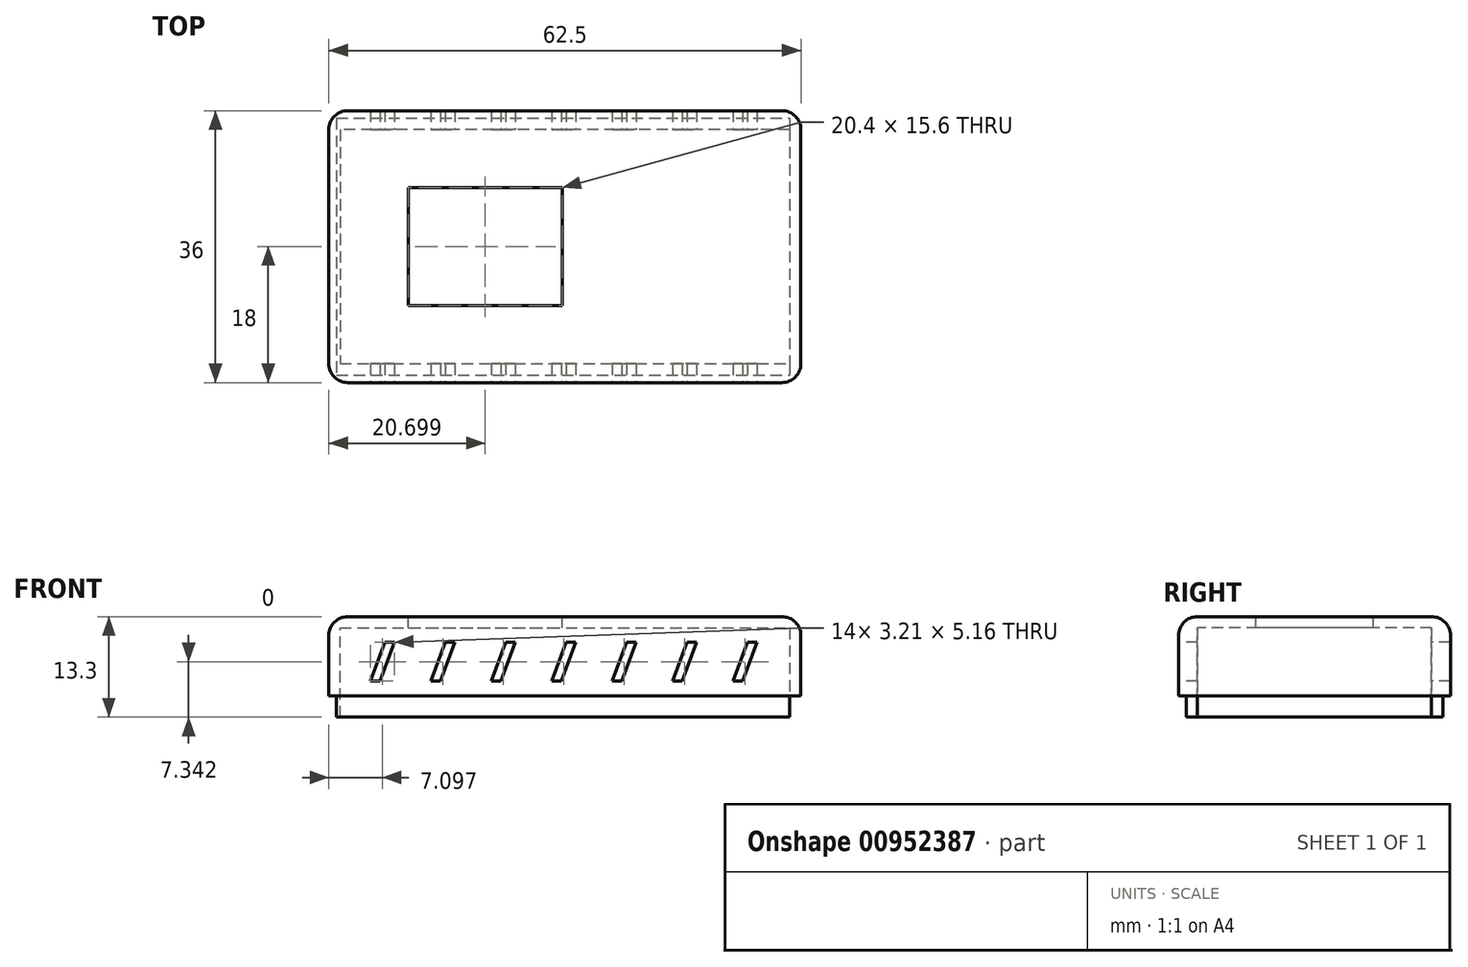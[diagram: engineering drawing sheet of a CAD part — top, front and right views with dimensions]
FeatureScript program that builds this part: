
annotation { "Feature Type Name" : "Feature", "Feature Type Description" : "" }
export const myFeature = defineFeature(function(context is Context, id is Id, definition is map)
    precondition{}
    {
        {
            var Q0;
            Q0=qCreatedBy(makeId("Top.planeOp"),FACE);
            var sketch = newSketch(context, id + "F0", { "sketchPlane" : qUnion([Q0])});
            skLineSegment(sketch, "E0.bottom", {"start": v(-31.16, 18) * mm, "end": v(31.34, 18) * mm});
            skLineSegment(sketch, "E0.top", {"start": v(-31.16, -18) * mm, "end": v(31.34, -18) * mm});
            skLineSegment(sketch, "E0.left", {"start": v(-31.16, 18) * mm, "end": v(-31.16, -18) * mm});
            skLineSegment(sketch, "E0.right", {"start": v(31.34, 18) * mm, "end": v(31.34, -18) * mm});
            skLineSegment(sketch, "E1.bottom", {"start": v(-30.16, 17) * mm, "end": v(29.84, 17) * mm});
            skLineSegment(sketch, "E1.top", {"start": v(-30.16, -17) * mm, "end": v(29.84, -17) * mm});
            skLineSegment(sketch, "E1.left", {"start": v(-30.16, 17) * mm, "end": v(-30.16, -17) * mm});
            skLineSegment(sketch, "E1.right", {"start": v(29.84, 17) * mm, "end": v(29.84, -17) * mm});
            skLineSegment(sketch, "E2", {"start": v(29.84, 15.5) * mm, "end": v(-28.66, 15.5) * mm});
            skLineSegment(sketch, "E3", {"start": v(-28.66, 15.5) * mm, "end": v(-28.66, -15.5) * mm});
            skLineSegment(sketch, "E4", {"start": v(-28.66, -15.5) * mm, "end": v(29.84, -15.5) * mm});
            skSolve(sketch);
        }
        {
            var Q0;
            {var subQ1=sQuery(id+"F0.wireOp",EDGE,"E1.bottom");Q0=makeQuery(id+"F0.imprint","IMPRINT",FACE,{"disambiguationData":[TD([[makeQuery(id+"F0.imprint","IMPRINT",EDGE,{"derivedFrom":subQ1}),-1.0]])]});}
            extrude(context, id + "F1", {"entities" : qUnion([Q0]), "oppositeDirection" : true, "offsetDistance" : 25 * mm, "depth" : 2.8 * mm});
        }
        {
            var Q0;
            Q0=makeQuery(id+"F0.imprint","IMPRINT",FACE,{"disambiguationData":[TD([[makeQuery(id+"F0.imprint","IMPRINT",EDGE,{"derivedFrom":sQuery(id+"F0.wireOp",EDGE,"E0.bottom")}),-1.0]])]});
            var Q1;
            {var subQ1=sQuery(id+"F0.wireOp",EDGE,"E1.bottom");Q1=makeQuery(id+"F0.imprint","IMPRINT",FACE,{"disambiguationData":[TD([[makeQuery(id+"F0.imprint","IMPRINT",EDGE,{"derivedFrom":subQ1}),-1.0]])]});}
            extrude(context, id + "F2", {"entities" : qUnion([Q0, Q1]), "operationType" : NewBodyOperationType.ADD, "offsetDistance" : 25 * mm, "depth" : 9 * mm});
        }
        {
            var Q0;
            Q0=makeQuery(id+"F2.opExtrude","SWEPT_FACE",FACE,{"disambiguationData":[OSD([sQuery(id+"F0.wireOp",EDGE,"E0.right")])]});
            var sketch = newSketch(context, id + "F3", { "sketchPlane" : qUnion([Q0])});
            skLineSegment(sketch, "E5.bottom", {"start": v(-18, 9) * mm, "end": v(18, 9) * mm});
            skLineSegment(sketch, "E5.top", {"start": v(-18, 10.5) * mm, "end": v(18, 10.5) * mm});
            skLineSegment(sketch, "E5.left", {"start": v(-18, 9) * mm, "end": v(-18, 10.5) * mm});
            skLineSegment(sketch, "E5.right", {"start": v(18, 9) * mm, "end": v(18, 10.5) * mm});
            skSolve(sketch);
        }
        {
            var Q0;
            Q0=makeQuery(id+"F3.imprint","IMPRINT",FACE,{"disambiguationData":[TD([[makeQuery(id+"F3.imprint","IMPRINT",EDGE,{"derivedFrom":sQuery(id+"F3.wireOp",EDGE,"E5.bottom")}),-1.0]])]});
            var Q1;
            Q1=qSketchRegion(id+"FGHyg4ucGbV6FiT_1",true);
            var Q2;
            Q2=makeQuery(id+"F2.opExtrude","SWEPT_FACE",FACE,{"disambiguationData":[OSD([sQuery(id+"F0.wireOp",EDGE,"E0.left")])]});
            extrude(context, id + "F4", {"entities" : qUnion([Q0, Q1]), "operationType" : NewBodyOperationType.ADD, "endBound" : BoundingType.UP_TO_SURFACE, "oppositeDirection" : true, "endBoundEntityFace" : qUnion([Q2]), "depth" : 62.3 * mm});
        }
        {
            var Q0;
            Q0=makeQuery(id+"F4.opExtrude","CAP_EDGE",EDGE,{"disambiguationData":[OSD([sQuery(id+"F3.wireOp",EDGE,"E5.top")])],"isStart":true});
            var Q1;
            Q1=makeQuery(id+"F4.opExtrude","SWEPT_EDGE",EDGE,{"disambiguationData":[OSD([sQuery(id+"F3.wireOp",EDGE,"E5.top"),sQuery(id+"F3.wireOp",EDGE,"E5.left")])]});
            var Q2;
            Q2=makeQuery(id+"F4.boolean.opBoolean","MERGE",EDGE,{"derivedFrom":[makeQuery(id+"F2.opExtrude","SWEPT_EDGE",EDGE,{"disambiguationData":[OSD([sQuery(id+"F0.wireOp",EDGE,"E0.top"),sQuery(id+"F0.wireOp",EDGE,"E0.right")])]}),makeQuery(id+"F4.opExtrude","CAP_EDGE",EDGE,{"disambiguationData":[OSD([sQuery(id+"F3.wireOp",EDGE,"E5.left")])],"isStart":true})]});
            var Q3;
            Q3=makeQuery(id+"F4.boolean.opBoolean","MERGE",EDGE,{"derivedFrom":[makeQuery(id+"F2.opExtrude","SWEPT_EDGE",EDGE,{"disambiguationData":[OSD([sQuery(id+"F0.wireOp",EDGE,"E0.bottom"),sQuery(id+"F0.wireOp",EDGE,"E0.right")])]}),makeQuery(id+"F4.opExtrude","CAP_EDGE",EDGE,{"disambiguationData":[OSD([sQuery(id+"F3.wireOp",EDGE,"E5.right")])],"isStart":true})]});
            var Q4;
            Q4=makeQuery(id+"F4.opExtrude","SWEPT_EDGE",EDGE,{"disambiguationData":[OSD([sQuery(id+"F3.wireOp",EDGE,"E5.top"),sQuery(id+"F3.wireOp",EDGE,"E5.right")])]});
            var Q5;
            Q5=makeQuery(id+"F4.boolean.opBoolean","MERGE",EDGE,{"derivedFrom":[makeQuery(id+"F2.opExtrude","SWEPT_EDGE",EDGE,{"disambiguationData":[OSD([sQuery(id+"F0.wireOp",EDGE,"E0.bottom"),sQuery(id+"F0.wireOp",EDGE,"E0.left")])]}),makeQuery(id+"F4.opExtrude","CAP_EDGE",EDGE,{"disambiguationData":[OSD([sQuery(id+"F3.wireOp",EDGE,"E5.right")])],"isStart":false})]});
            var Q6;
            Q6=makeQuery(id+"F4.opExtrude","CAP_EDGE",EDGE,{"disambiguationData":[OSD([sQuery(id+"F3.wireOp",EDGE,"E5.top")])],"isStart":false});
            var Q7;
            Q7=makeQuery(id+"F4.boolean.opBoolean","MERGE",EDGE,{"derivedFrom":[makeQuery(id+"F2.opExtrude","SWEPT_EDGE",EDGE,{"disambiguationData":[OSD([sQuery(id+"F0.wireOp",EDGE,"E0.top"),sQuery(id+"F0.wireOp",EDGE,"E0.left")])]}),makeQuery(id+"F4.opExtrude","CAP_EDGE",EDGE,{"disambiguationData":[OSD([sQuery(id+"F3.wireOp",EDGE,"E5.left")])],"isStart":false})]});
            fillet(context, id + "F5", {"entities" : qUnion([Q0, Q1, Q2, Q3, Q4, Q5, Q6, Q7]), "radius" : 2.5 * mm, "tangentPropagation" : true, "allowEdgeOverflow" : false});
        }
        {
            var Q0;
            {var subQ0=sQuery(id+"F0.wireOp",EDGE,"E3");Q0=makeQuery(id+"FEPfuos01jypXZx_1.boolean.opBoolean","SPLIT",FACE,{"disambiguationData":[TD([makeQuery(id+"FEPfuos01jypXZx_1.opExtrude","SWEPT_FACE",FACE,{"disambiguationData":[OSD([sQuery(id+"FNJi3SJlg6xjIKS_1.wireOp",EDGE,"CGCuMa7v-HkjL-wQTo-F6Tt-e60EdCvoSJhP.bottom")])]})])],"derivedFrom":makeQuery(id+"F2.boolean.opBoolean","MERGE",FACE,{"derivedFrom":[makeQuery(id+"F1.opExtrude","SWEPT_FACE",FACE,{"disambiguationData":[OSD([subQ0])]}),makeQuery(id+"F2.opExtrude","SWEPT_FACE",FACE,{"disambiguationData":[OSD([subQ0])]})]})});}
            extrude(context, id + "F6", {"entities" : qUnion([Q0]), "operationType" : NewBodyOperationType.REMOVE, "oppositeDirection" : true, "depth" : 1 * mm});
        }
        {
            var Q0;
            Q0=makeQuery(id+"F4.opExtrude","SWEPT_FACE",FACE,{"disambiguationData":[OSD([sQuery(id+"F3.wireOp",EDGE,"E5.top")])]});
            var sketch = newSketch(context, id + "F9", { "sketchPlane" : qUnion([Q0])});
            skLineSegment(sketch, "E6.bottom", {"start": v(-20.66, 7.8) * mm, "end": v(-0.26, 7.8) * mm});
            skLineSegment(sketch, "E6.top", {"start": v(-20.66, -7.8) * mm, "end": v(-0.26, -7.8) * mm});
            skLineSegment(sketch, "E6.left", {"start": v(-20.66, 7.8) * mm, "end": v(-20.66, -7.8) * mm});
            skLineSegment(sketch, "E6.right", {"start": v(-0.26, 7.8) * mm, "end": v(-0.26, -7.8) * mm});
            skSolve(sketch);
        }
        {
            var Q0;
            Q0=makeQuery(id+"F9.imprint","IMPRINT",FACE,{"disambiguationData":[TD([[makeQuery(id+"F9.imprint","IMPRINT",EDGE,{"derivedFrom":sQuery(id+"F9.wireOp",EDGE,"E6.bottom")}),-1.0]])]});
            extrude(context, id + "F10", {"entities" : qUnion([Q0]), "operationType" : NewBodyOperationType.REMOVE, "endBound" : BoundingType.THROUGH_ALL, "oppositeDirection" : true, "depth" : 2 * mm, "offsetDistance" : 25 * mm});
        }
        {
            var Q0;
            Q0=makeQuery(id+"F4.boolean.opBoolean","MERGE",FACE,{"derivedFrom":[makeQuery(id+"F2.opExtrude","SWEPT_FACE",FACE,{"disambiguationData":[OSD([sQuery(id+"F0.wireOp",EDGE,"E0.top")])]}),makeQuery(id+"F4.opExtrude","SWEPT_FACE",FACE,{"disambiguationData":[OSD([sQuery(id+"F3.wireOp",EDGE,"E5.left")])]})]});
            var sketch = newSketch(context, id + "F11", { "sketchPlane" : qUnion([Q0])});
            skLineSegment(sketch, "E7", {"start": v(-25.67, 1.96) * mm, "end": v(-23.72, 7.12) * mm});
            skLineSegment(sketch, "E8", {"start": v(-23.72, 7.12) * mm, "end": v(-22.46, 7.12) * mm});
            skLineSegment(sketch, "E9", {"start": v(-22.46, 7.12) * mm, "end": v(-24.4, 1.96) * mm});
            skLineSegment(sketch, "E10", {"start": v(-24.4, 1.96) * mm, "end": v(-25.67, 1.96) * mm});
            skLineSegment(sketch, "E11.1.0.0", {"start": v(-17.67, 1.96) * mm, "end": v(-15.72, 7.12) * mm});
            skLineSegment(sketch, "E11.1.0.1", {"start": v(-14.46, 7.12) * mm, "end": v(-16.4, 1.96) * mm});
            skLineSegment(sketch, "E11.1.0.2", {"start": v(-15.72, 7.12) * mm, "end": v(-14.46, 7.12) * mm});
            skLineSegment(sketch, "E11.1.0.3", {"start": v(-16.4, 1.96) * mm, "end": v(-17.67, 1.96) * mm});
            skLineSegment(sketch, "E11.2.0.0", {"start": v(-9.67, 1.96) * mm, "end": v(-7.72, 7.12) * mm});
            skLineSegment(sketch, "E11.2.0.1", {"start": v(-6.46, 7.12) * mm, "end": v(-8.4, 1.96) * mm});
            skLineSegment(sketch, "E11.2.0.2", {"start": v(-7.72, 7.12) * mm, "end": v(-6.46, 7.12) * mm});
            skLineSegment(sketch, "E11.2.0.3", {"start": v(-8.4, 1.96) * mm, "end": v(-9.67, 1.96) * mm});
            skLineSegment(sketch, "E11.3.0.0", {"start": v(-1.67, 1.96) * mm, "end": v(0.28, 7.12) * mm});
            skLineSegment(sketch, "E11.3.0.1", {"start": v(1.54, 7.12) * mm, "end": v(-0.4, 1.96) * mm});
            skLineSegment(sketch, "E11.3.0.2", {"start": v(0.28, 7.12) * mm, "end": v(1.54, 7.12) * mm});
            skLineSegment(sketch, "E11.3.0.3", {"start": v(-0.4, 1.96) * mm, "end": v(-1.67, 1.96) * mm});
            skLineSegment(sketch, "E11.4.0.0", {"start": v(6.33, 1.96) * mm, "end": v(8.28, 7.12) * mm});
            skLineSegment(sketch, "E11.4.0.1", {"start": v(9.54, 7.12) * mm, "end": v(7.6, 1.96) * mm});
            skLineSegment(sketch, "E11.4.0.2", {"start": v(8.28, 7.12) * mm, "end": v(9.54, 7.12) * mm});
            skLineSegment(sketch, "E11.4.0.3", {"start": v(7.6, 1.96) * mm, "end": v(6.33, 1.96) * mm});
            skLineSegment(sketch, "E11.5.0.0", {"start": v(14.33, 1.96) * mm, "end": v(16.28, 7.12) * mm});
            skLineSegment(sketch, "E11.5.0.1", {"start": v(17.54, 7.12) * mm, "end": v(15.6, 1.96) * mm});
            skLineSegment(sketch, "E11.5.0.2", {"start": v(16.28, 7.12) * mm, "end": v(17.54, 7.12) * mm});
            skLineSegment(sketch, "E11.5.0.3", {"start": v(15.6, 1.96) * mm, "end": v(14.33, 1.96) * mm});
            skLineSegment(sketch, "E11.6.0.0", {"start": v(22.33, 1.96) * mm, "end": v(24.28, 7.12) * mm});
            skLineSegment(sketch, "E11.6.0.1", {"start": v(25.54, 7.12) * mm, "end": v(23.6, 1.96) * mm});
            skLineSegment(sketch, "E11.6.0.2", {"start": v(24.28, 7.12) * mm, "end": v(25.54, 7.12) * mm});
            skLineSegment(sketch, "E11.6.0.3", {"start": v(23.6, 1.96) * mm, "end": v(22.33, 1.96) * mm});
            skLineSegment(sketch, "E11.direction1", {"start": v(-25.67, 1.96) * mm, "end": v(-17.67, 1.96) * mm, "construction": true});
            skSolve(sketch);
        }
        {
            var Q0;
            Q0 = qSketchRegion(id + "F11", true);
            extrude(context, id + "F12", {"entities" : qUnion([Q0]), "operationType" : NewBodyOperationType.REMOVE, "oppositeDirection" : true, "depth" : 50 * mm, "offsetDistance" : 25 * mm});
        }
    });
